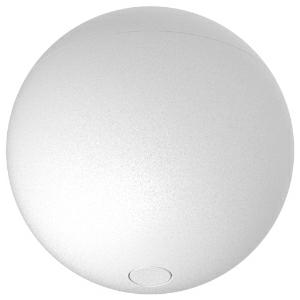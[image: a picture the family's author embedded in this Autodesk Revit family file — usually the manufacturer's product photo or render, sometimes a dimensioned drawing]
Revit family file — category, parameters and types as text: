
# Revit family: snooker_dekor__810-0316
name_source: partatom
category: Leuchten
revit_build: Autodesk Revit 2016 (Build: 20190508_0715(x64)
units: mm (PartAtom-declared; Revit-internal decimal feet)

## family parameters
Basisbauteil = Fläche
Beim Laden mit Abzugskörper schneiden = Nein
Bemaßung runder Anschluss = Durchmesser verwenden
Gemeinsam genutzt = Nein
Lichtquelle = Nein
Raumberechnungspunkt = Nein
Teiletyp = Normal

## types (1)
- 810-0316-
    Beschreibung = The article can be powder coated in 29 colours. The integrated ballast allows for an operation with.
    Height = 71 mm
    Hersteller = Prolicht
    Lampe = 0 x
    Length = 72 mm
    Luminous efficacy = 0 lm/W
    ModVariant = Nein
    Modell = 810-0316
    Number of Poles = 1
    OnlyDefault = Ja
    Power Factor = 1
    Product Name = SNOOKER DEKOR
    Product group = Luminaires
    ProductGroupID = 0
    Protection Class = Protection class
    Protection Degree = Degree of protection
    RLX_Detail_Level = 1
    RlxData = <blob elided: 95113 chars, md5=0ce941fd>
    Scheinlast = 0 VA
    Standby Power = 0 W
    System Light Flux = 0 lm
    System Power = 0 W
    Typenbild = 810-0316.jpg
    URL = http://relux.com
    VarID = 810-0316-
    Voltage = 0 V
    Vorgabe-Ansicht = 1800 mm
    Weight = 0.00 kg
    Width = 0 mm  [stored 0 ft]

note: [stored X ft] marks values corroborated as IEEE doubles in the binary element streams (Revit-internal decimal feet)

## geometry (parser evidence)
native form markers: Blend x4, Sweep x11
no freeform markers — native parametric forms only
